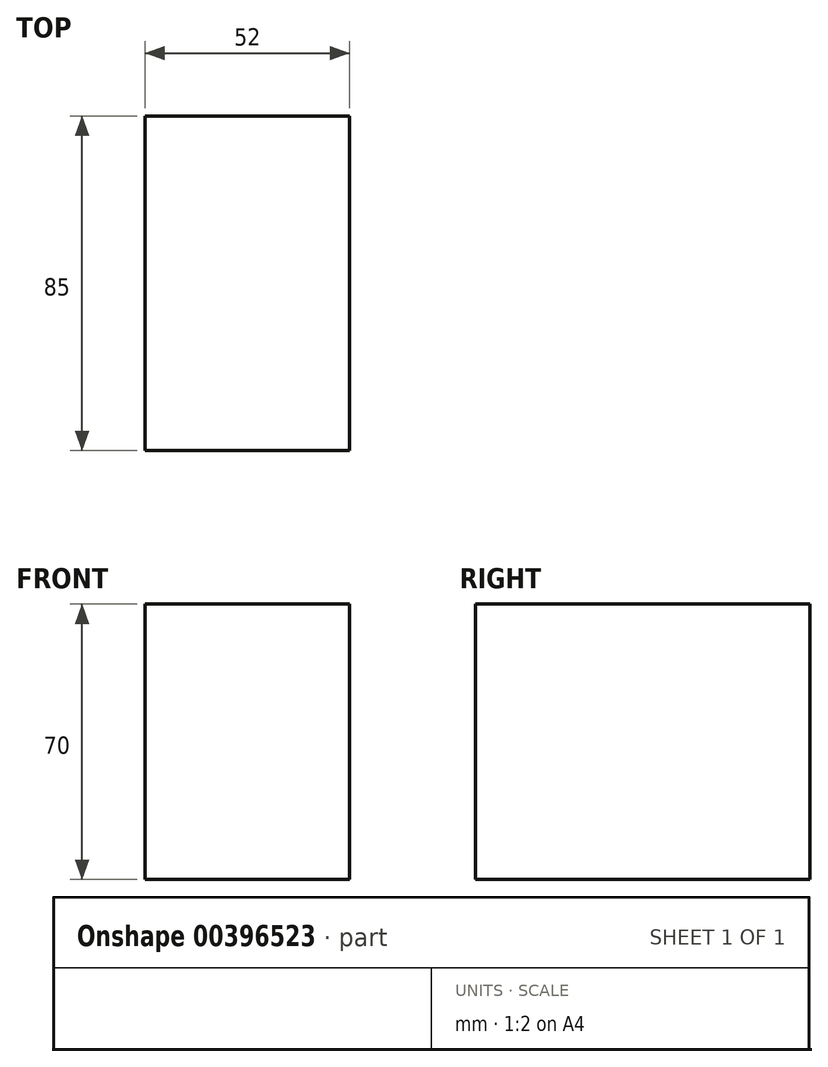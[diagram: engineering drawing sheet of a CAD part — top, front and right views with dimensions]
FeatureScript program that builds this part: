
annotation { "Feature Type Name" : "Feature", "Feature Type Description" : "" }
export const myFeature = defineFeature(function(context is Context, id is Id, definition is map)
    precondition{}
    {
        {
            var Q0;
            Q0=qCreatedBy(makeId("Front.planeOp"),FACE);
            var sketch = newSketch(context, id + "F0", { "sketchPlane" : qUnion([Q0])});
            skLineSegment(sketch, "E0.bottom", {"start": v(26, -35) * mm, "end": v(-26, -35) * mm});
            skLineSegment(sketch, "E0.top", {"start": v(26, 35) * mm, "end": v(-26, 35) * mm});
            skLineSegment(sketch, "E0.left", {"start": v(26, -35) * mm, "end": v(26, 35) * mm});
            skLineSegment(sketch, "E0.right", {"start": v(-26, -35) * mm, "end": v(-26, 35) * mm});
            skPoint(sketch, "E0.middle", {"position": v(0, 0) * mm});
            skSolve(sketch);
        }
        {
            var Q0;
            Q0=makeQuery(id+"F0.imprint","IMPRINT",FACE,{"disambiguationData":[TD([[makeQuery(id+"F0.imprint","IMPRINT",EDGE,{"derivedFrom":sQuery(id+"F0.wireOp",EDGE,"E0.bottom")}),-1.0]])]});
            extrude(context, id + "F1", {"entities" : qUnion([Q0]), "depth" : 85 * mm});
        }
    });
